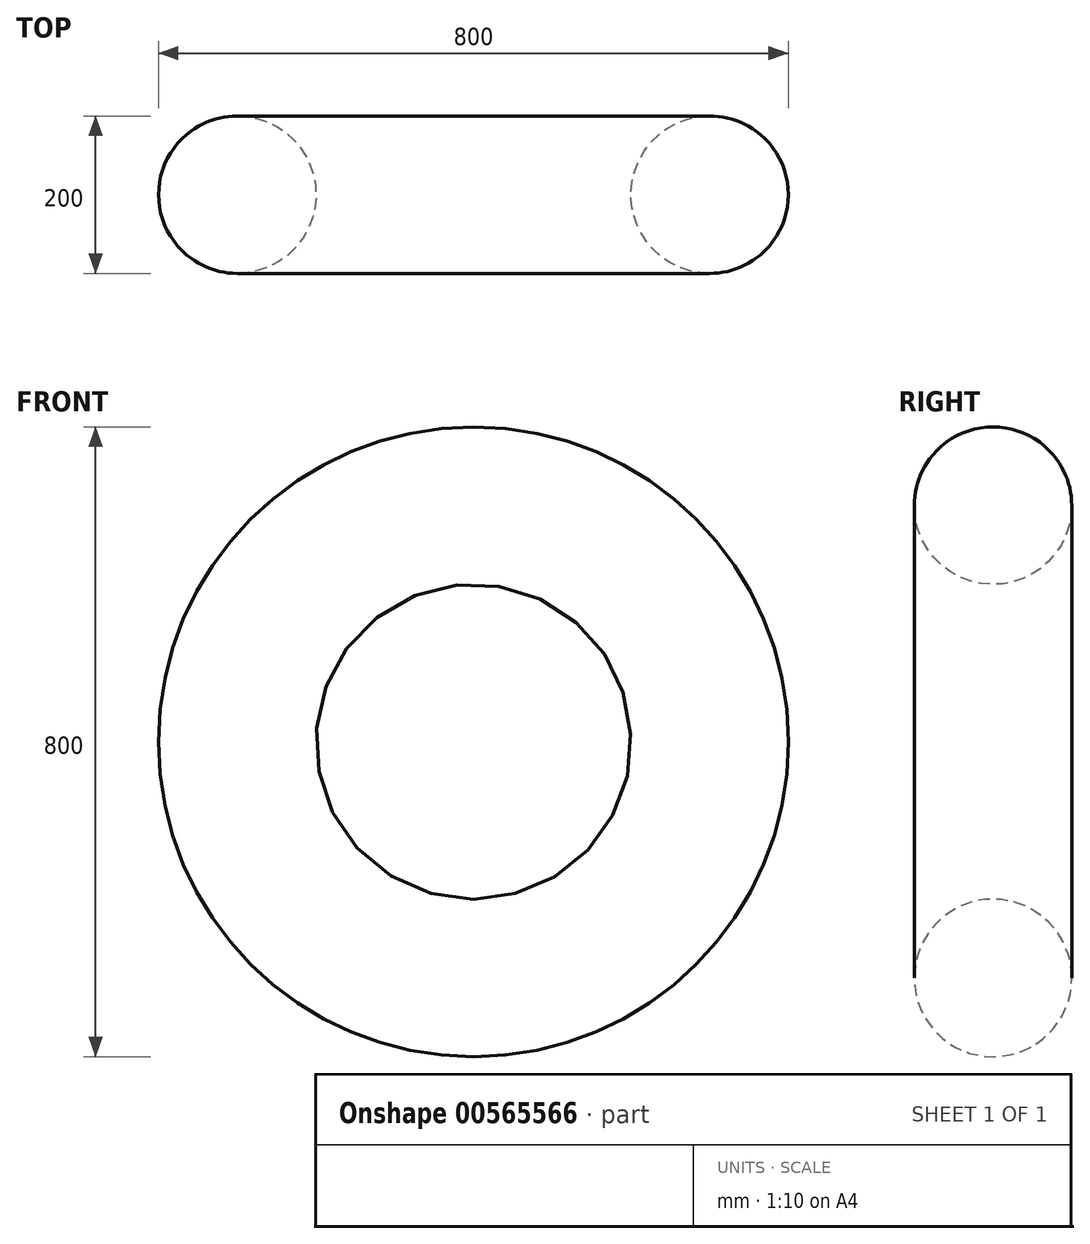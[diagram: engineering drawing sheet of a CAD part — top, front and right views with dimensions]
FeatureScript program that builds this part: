
annotation { "Feature Type Name" : "Feature", "Feature Type Description" : "" }
export const myFeature = defineFeature(function(context is Context, id is Id, definition is map)
    precondition{}
    {
        {
            var Q0;
            Q0=qCreatedBy(makeId("Top.planeOp"),FACE);
            var sketch = newSketch(context, id + "F0", { "sketchPlane" : qUnion([Q0])});
            skCircle(sketch, "E0", {"center": v(300, 0) * mm, "radius": 100 * mm});
            skSolve(sketch);
        }
        {
            var Q0;
            Q0=qCreatedBy(makeId("Top.planeOp"),FACE);
            var sketch = newSketch(context, id + "F1", { "sketchPlane" : qUnion([Q0])});
            skLineSegment(sketch, "E1", {"start": v(0, 0) * mm, "end": v(0, 159.9) * mm});
            skSolve(sketch);
        }
        {
            var Q0;
            Q0=makeQuery(id+"F0.imprint","IMPRINT",FACE,{"disambiguationData":[TD([[makeQuery(id+"F0.imprint","IMPRINT",EDGE,{"derivedFrom":sQuery(id+"F0.wireOp",EDGE,"E0")}),1.0]])]});
            var Q1;
            Q1 = qSketchRegion(id + "F0", true);
            var Q2;
            Q2=sQuery(id+"F1.wireOp",EDGE,"E1");
            revolve(context, id + "F2", {"entities" : qUnion([Q0, Q1]), "axis" : qUnion([Q2]), "revolveType" : RevolveType.FULL});
        }
    });
